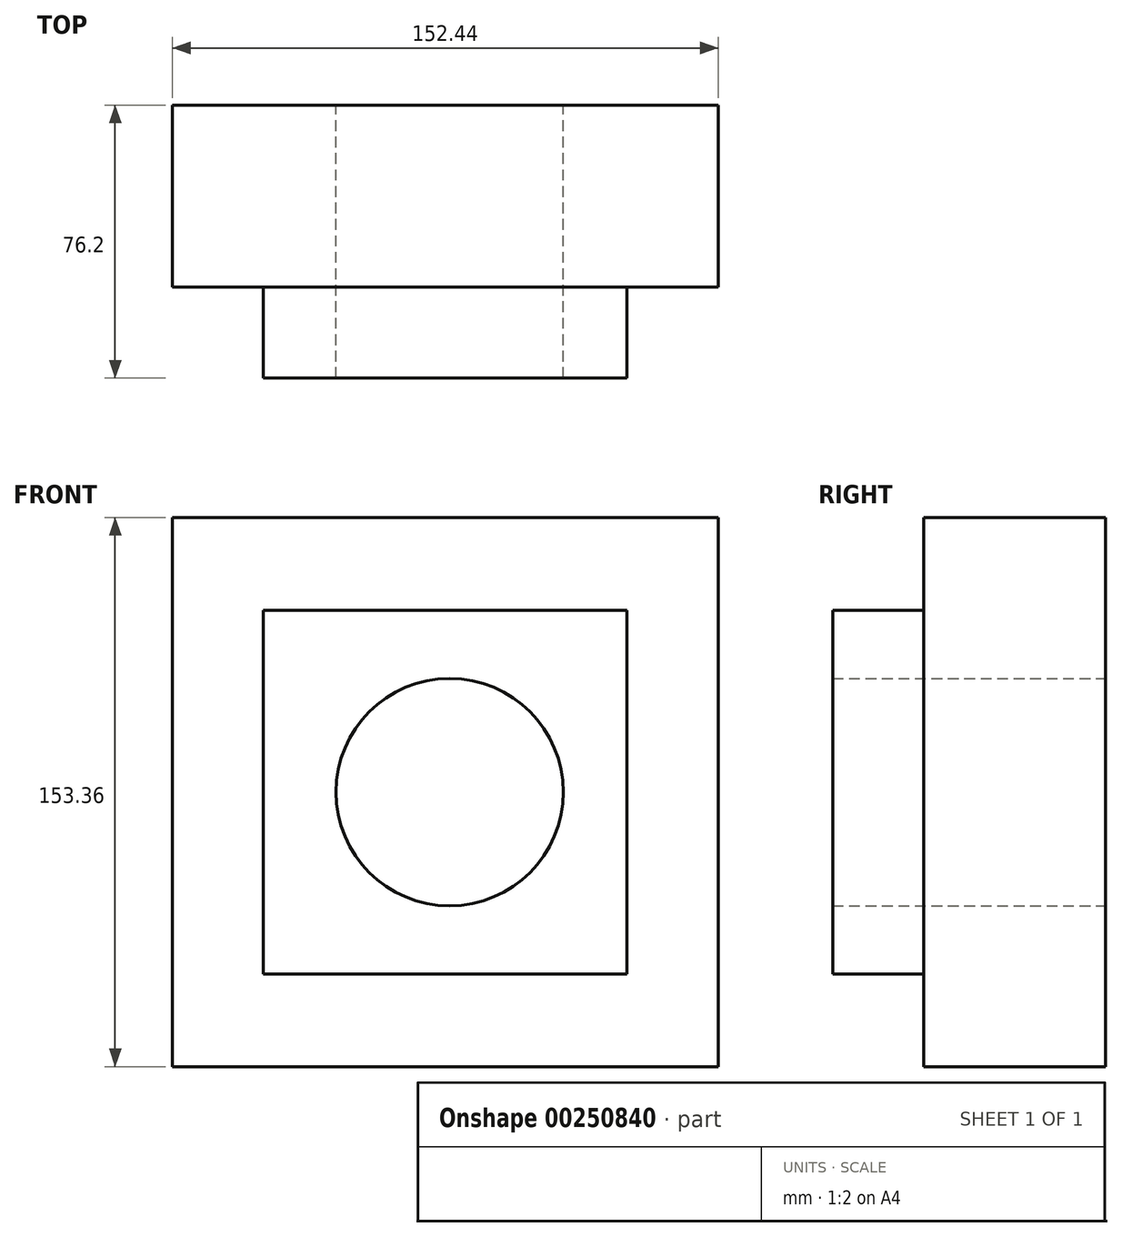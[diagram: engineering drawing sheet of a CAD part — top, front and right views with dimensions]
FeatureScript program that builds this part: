
annotation { "Feature Type Name" : "Feature", "Feature Type Description" : "" }
export const myFeature = defineFeature(function(context is Context, id is Id, definition is map)
    precondition{}
    {
        {
            var Q0;
            Q0=qCreatedBy(makeId("Front.planeOp"),FACE);
            var sketch = newSketch(context, id + "F0", { "sketchPlane" : qUnion([Q0])});
            skCircle(sketch, "E0", {"center": v(1.2, 0) * mm, "radius": 31.75 * mm});
            skLineSegment(sketch, "E1.bottom", {"start": v(50.8, 50.8) * mm, "end": v(-50.8, 50.8) * mm});
            skLineSegment(sketch, "E1.top", {"start": v(50.8, -50.8) * mm, "end": v(-50.8, -50.8) * mm});
            skLineSegment(sketch, "E1.left", {"start": v(50.8, 50.8) * mm, "end": v(50.8, -50.8) * mm});
            skLineSegment(sketch, "E1.right", {"start": v(-50.8, 50.8) * mm, "end": v(-50.8, -50.8) * mm});
            skPoint(sketch, "E1.middle", {"position": v(0, 0) * mm});
            skLineSegment(sketch, "E2.bottom", {"start": v(76.22, 76.68) * mm, "end": v(-76.22, 76.68) * mm});
            skLineSegment(sketch, "E2.top", {"start": v(76.22, -76.68) * mm, "end": v(-76.22, -76.68) * mm});
            skLineSegment(sketch, "E2.left", {"start": v(76.22, 76.68) * mm, "end": v(76.22, -76.68) * mm});
            skLineSegment(sketch, "E2.right", {"start": v(-76.22, 76.68) * mm, "end": v(-76.22, -76.68) * mm});
            skSolve(sketch);
        }
        {
            var Q0;
            Q0=makeQuery(id+"F0.imprint","IMPRINT",FACE,{"disambiguationData":[TD([[makeQuery(id+"F0.imprint","IMPRINT",EDGE,{"derivedFrom":sQuery(id+"F0.wireOp",EDGE,"E0")}),-1.0]])]});
            extrude(context, id + "F1", {"entities" : qUnion([Q0]), "depth" : 76.2 * mm});
        }
        {
            var Q0;
            Q0=makeQuery(id+"F0.imprint","IMPRINT",FACE,{"disambiguationData":[TD([[makeQuery(id+"F0.imprint","IMPRINT",EDGE,{"derivedFrom":sQuery(id+"F0.wireOp",EDGE,"E1.bottom")}),-1.0]])]});
            extrude(context, id + "F2", {"entities" : qUnion([Q0]), "operationType" : NewBodyOperationType.ADD, "depth" : 50.8 * mm});
        }
    });
